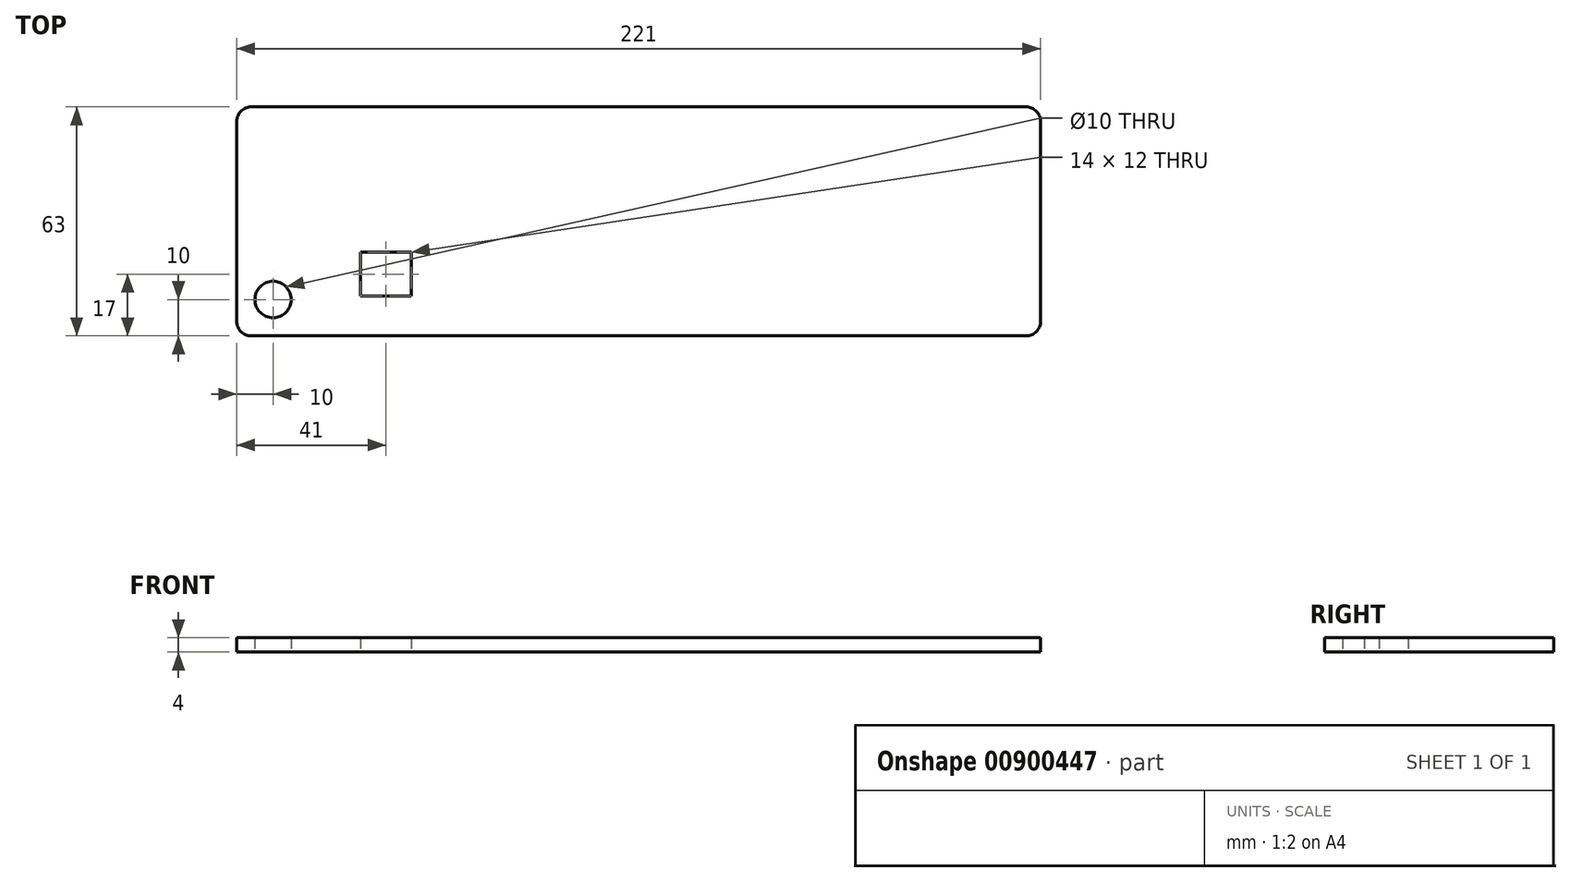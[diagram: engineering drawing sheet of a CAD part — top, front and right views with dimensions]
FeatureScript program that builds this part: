
annotation { "Feature Type Name" : "Feature", "Feature Type Description" : "" }
export const myFeature = defineFeature(function(context is Context, id is Id, definition is map)
    precondition{}
    {
        {
            var Q0;
            Q0=qCreatedBy(makeId("Top.planeOp"),FACE);
            var sketch = newSketch(context, id + "F0", { "sketchPlane" : qUnion([Q0])});
            skLineSegment(sketch, "E0.bottom", {"start": v(-110.5, 31.5) * mm, "end": v(110.5, 31.5) * mm});
            skLineSegment(sketch, "E0.top", {"start": v(-110.5, -31.5) * mm, "end": v(110.5, -31.5) * mm});
            skLineSegment(sketch, "E0.left", {"start": v(-110.5, 31.5) * mm, "end": v(-110.5, -31.5) * mm});
            skLineSegment(sketch, "E0.right", {"start": v(110.5, 31.5) * mm, "end": v(110.5, -31.5) * mm});
            skLineSegment(sketch, "E1", {"start": v(-130.15, 0) * mm, "end": v(168.49, 0) * mm, "construction": true});
            skCircle(sketch, "E2", {"center": v(-100.5, -21.5) * mm, "radius": 5 * mm});
            skLineSegment(sketch, "E3.bottom", {"start": v(-76.5, -20.5) * mm, "end": v(-62.5, -20.5) * mm});
            skLineSegment(sketch, "E3.top", {"start": v(-76.5, -8.5) * mm, "end": v(-62.5, -8.5) * mm});
            skLineSegment(sketch, "E3.left", {"start": v(-76.5, -20.5) * mm, "end": v(-76.5, -8.5) * mm});
            skLineSegment(sketch, "E3.right", {"start": v(-62.5, -20.5) * mm, "end": v(-62.5, -8.5) * mm});
            skSolve(sketch);
        }
        {
            var Q0;
            Q0 = qSketchRegion(id + "F0", true);
            extrude(context, id + "F1", {"entities" : qUnion([Q0]), "depth" : 4 * mm, "offsetDistance" : 25 * mm});
        }
        {
            var Q0;
            Q0=makeQuery(id+"F1.opExtrude","SWEPT_EDGE",EDGE,{"disambiguationData":[OSD([sQuery(id+"F0.wireOp",EDGE,"E0.bottom"),sQuery(id+"F0.wireOp",EDGE,"E0.right")])]});
            var Q1;
            Q1=makeQuery(id+"F1.opExtrude","SWEPT_EDGE",EDGE,{"disambiguationData":[OSD([sQuery(id+"F0.wireOp",EDGE,"E0.top"),sQuery(id+"F0.wireOp",EDGE,"E0.right")])]});
            var Q2;
            Q2=makeQuery(id+"F1.opExtrude","SWEPT_EDGE",EDGE,{"disambiguationData":[OSD([sQuery(id+"F0.wireOp",EDGE,"E0.top"),sQuery(id+"F0.wireOp",EDGE,"E0.left")])]});
            var Q3;
            Q3=makeQuery(id+"F1.opExtrude","SWEPT_EDGE",EDGE,{"disambiguationData":[OSD([sQuery(id+"F0.wireOp",EDGE,"E0.bottom"),sQuery(id+"F0.wireOp",EDGE,"E0.left")])]});
            fillet(context, id + "F2", {"entities" : qUnion([Q0, Q1, Q2, Q3]), "radius" : 4 * mm, "tangentPropagation" : true, "allowEdgeOverflow" : false});
        }
    });
